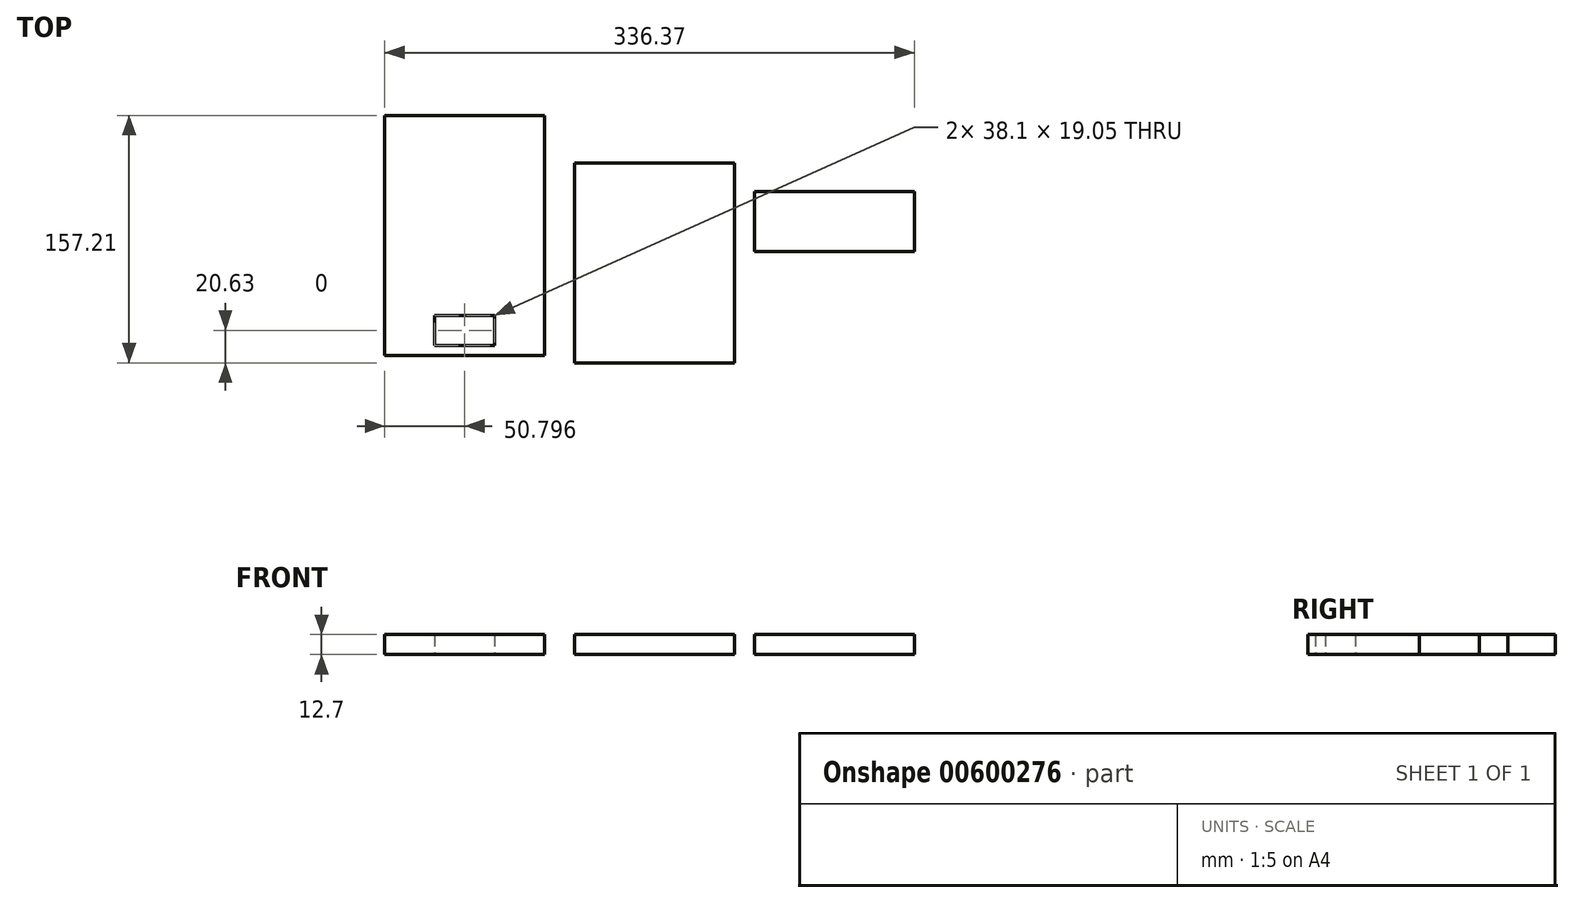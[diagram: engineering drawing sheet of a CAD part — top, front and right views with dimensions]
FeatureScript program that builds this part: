
annotation { "Feature Type Name" : "Feature", "Feature Type Description" : "" }
export const myFeature = defineFeature(function(context is Context, id is Id, definition is map)
    precondition{}
    {
        {
            var Q0;
            Q0=qCreatedBy(makeId("Top.planeOp"),FACE);
            var sketch = newSketch(context, id + "F0", { "sketchPlane" : qUnion([Q0])});
            skLineSegment(sketch, "E0.bottom", {"start": v(53.37, -63.5) * mm, "end": v(-48.23, -63.5) * mm});
            skLineSegment(sketch, "E0.top", {"start": v(53.37, 63.5) * mm, "end": v(-48.23, 63.5) * mm});
            skLineSegment(sketch, "E0.left", {"start": v(53.37, -63.5) * mm, "end": v(53.37, 63.5) * mm});
            skLineSegment(sketch, "E0.right", {"start": v(-48.23, -63.5) * mm, "end": v(-48.23, 63.5) * mm});
            skPoint(sketch, "E0.middle", {"position": v(2.57, 0) * mm});
            skLineSegment(sketch, "E1.bottom", {"start": v(-67.1, -58.7) * mm, "end": v(-168.7, -58.7) * mm});
            skLineSegment(sketch, "E1.top", {"start": v(-67.1, 93.7) * mm, "end": v(-168.7, 93.7) * mm});
            skLineSegment(sketch, "E1.left", {"start": v(-67.1, -58.7) * mm, "end": v(-67.1, 93.7) * mm});
            skLineSegment(sketch, "E1.right", {"start": v(-168.7, -58.7) * mm, "end": v(-168.7, 93.7) * mm});
            skPoint(sketch, "E1.middle", {"position": v(-117.9, 17.5) * mm});
            skLineSegment(sketch, "E2.bottom", {"start": v(167.67, 7.2) * mm, "end": v(66.07, 7.2) * mm});
            skLineSegment(sketch, "E2.top", {"start": v(167.67, 45.3) * mm, "end": v(66.07, 45.3) * mm});
            skLineSegment(sketch, "E2.left", {"start": v(167.67, 7.2) * mm, "end": v(167.67, 45.3) * mm});
            skLineSegment(sketch, "E2.right", {"start": v(66.07, 7.2) * mm, "end": v(66.07, 45.3) * mm});
            skPoint(sketch, "E2.middle", {"position": v(116.87, 26.26) * mm});
            skLineSegment(sketch, "E3.bottom", {"start": v(-98.85, -33.34) * mm, "end": v(-136.95, -33.34) * mm});
            skLineSegment(sketch, "E3.top", {"start": v(-98.85, -52.4) * mm, "end": v(-136.95, -52.4) * mm});
            skLineSegment(sketch, "E3.left", {"start": v(-98.85, -33.34) * mm, "end": v(-98.85, -52.4) * mm});
            skLineSegment(sketch, "E3.right", {"start": v(-136.95, -33.34) * mm, "end": v(-136.95, -52.4) * mm});
            skPoint(sketch, "E3.middle", {"position": v(-117.9, -42.87) * mm});
            skSolve(sketch);
        }
        {
            var Q0;
            Q0=makeQuery(id+"F0.imprint","IMPRINT",FACE,{"disambiguationData":[TD([[makeQuery(id+"F0.imprint","IMPRINT",EDGE,{"derivedFrom":sQuery(id+"F0.wireOp",EDGE,"E1.bottom")}),-1.0]])]});
            var Q1;
            Q1=makeQuery(id+"F0.imprint","IMPRINT",FACE,{"disambiguationData":[TD([[makeQuery(id+"F0.imprint","IMPRINT",EDGE,{"derivedFrom":sQuery(id+"F0.wireOp",EDGE,"E0.bottom")}),-1.0]])]});
            var Q2;
            Q2=makeQuery(id+"F0.imprint","IMPRINT",FACE,{"disambiguationData":[TD([[makeQuery(id+"F0.imprint","IMPRINT",EDGE,{"derivedFrom":sQuery(id+"F0.wireOp",EDGE,"E2.bottom")}),-1.0]])]});
            extrude(context, id + "F1", {"entities" : qUnion([Q0, Q1, Q2]), "depth" : 12.7 * mm, "offsetDistance" : 25.4 * mm});
        }
    });
